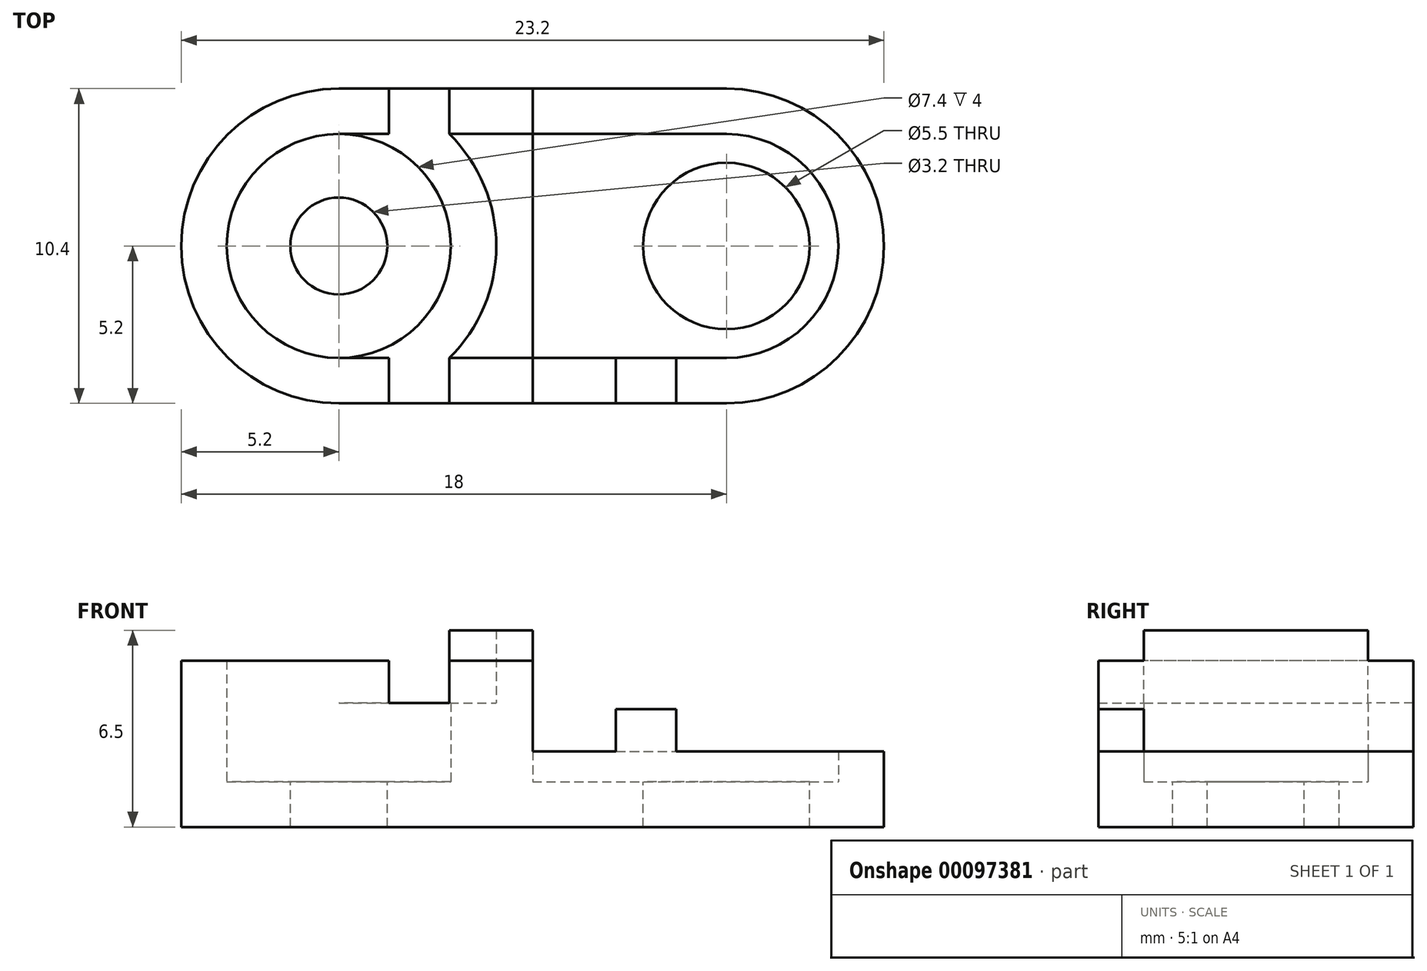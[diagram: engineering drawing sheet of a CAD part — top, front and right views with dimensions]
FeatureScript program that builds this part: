
annotation { "Feature Type Name" : "Feature", "Feature Type Description" : "" }
export const myFeature = defineFeature(function(context is Context, id is Id, definition is map)
    precondition{}
    {
        {
            var Q0;
            Q0=qCreatedBy(makeId("Top.planeOp"),FACE);
            var sketch = newSketch(context, id + "F0", { "sketchPlane" : qUnion([Q0])});
            skArc(sketch, "E0", {"start": v(-6.4, 5.2) * mm, "mid": v(-11.6, 0) * mm, "end": v(-6.4, -5.2) * mm});
            skArc(sketch, "E1", {"start": v(6.4, -5.2) * mm, "mid": v(11.6, 0) * mm, "end": v(6.4, 5.2) * mm});
            skLineSegment(sketch, "E2", {"start": v(0, -5.2) * mm, "end": v(0, 5.2) * mm, "construction": true});
            skLineSegment(sketch, "E3", {"start": v(-6.4, 5.2) * mm, "end": v(6.4, 5.2) * mm});
            skLineSegment(sketch, "E4", {"start": v(-6.4, -5.2) * mm, "end": v(6.4, -5.2) * mm});
            skSolve(sketch);
        }
        {
            var Q0;
            Q0 = qSketchRegion(id + "F0", true);
            extrude(context, id + "F1", {"entities" : qUnion([Q0]), "depth" : 1.5 * mm});
        }
        {
            var Q0;
            Q0=makeQuery(id+"F1.opExtrude","CAP_FACE",FACE,{"disambiguationData":[OSD([sQuery(id+"F0.wireOp",EDGE,"E0"),sQuery(id+"F0.wireOp",EDGE,"E1"),sQuery(id+"F0.wireOp",EDGE,"E3"),sQuery(id+"F0.wireOp",EDGE,"E4")])],"isStart":false});
            var sketch = newSketch(context, id + "F2", { "sketchPlane" : qUnion([Q0])});
            skLineSegment(sketch, "E5.0", {"start": v(-6.4, 5.2) * mm, "end": v(6.4, 5.2) * mm});
            skArc(sketch, "E5.1", {"start": v(-6.4, 5.2) * mm, "mid": v(-11.6, 0) * mm, "end": v(-6.4, -5.2) * mm});
            skLineSegment(sketch, "E5.2", {"start": v(-6.4, -5.2) * mm, "end": v(6.4, -5.2) * mm});
            skArc(sketch, "E5.3", {"start": v(6.4, -5.2) * mm, "mid": v(11.6, 0) * mm, "end": v(6.4, 5.2) * mm});
            skArc(sketch, "E6.0", {"start": v(-6.4, 3.7) * mm, "mid": v(-10.1, 0) * mm, "end": v(-6.4, -3.7) * mm});
            skLineSegment(sketch, "E6.1", {"start": v(-6.4, 3.7) * mm, "end": v(6.4, 3.7) * mm});
            skArc(sketch, "E6.2", {"start": v(6.4, -3.7) * mm, "mid": v(10.1, 0) * mm, "end": v(6.4, 3.7) * mm});
            skLineSegment(sketch, "E6.3", {"start": v(-6.4, -3.7) * mm, "end": v(6.4, -3.7) * mm});
            skLineSegment(sketch, "E7", {"start": v(0, -5.2) * mm, "end": v(0, -3.7) * mm});
            skLineSegment(sketch, "E8", {"start": v(0, -3.7) * mm, "end": v(0, 3.7) * mm, "construction": true});
            skLineSegment(sketch, "E9", {"start": v(0, 3.7) * mm, "end": v(0, 5.2) * mm});
            skSolve(sketch);
        }
        {
            var Q0;
            {var subQ3=sQuery(id+"F2.wireOp",EDGE,"E5.1");Q0=makeQuery(id+"F2.imprint","IMPRINT",FACE,{"disambiguationData":[TD([[makeQuery(id+"F2.imprint","IMPRINT",EDGE,{"derivedFrom":subQ3}),1.0]])]});}
            extrude(context, id + "F3", {"entities" : qUnion([Q0]), "operationType" : NewBodyOperationType.ADD, "depth" : 4 * mm});
        }
        {
            var Q0;
            {var subQ0=sQuery(id+"F2.wireOp",EDGE,"E5.3");Q0=makeQuery(id+"F2.imprint","IMPRINT",FACE,{"disambiguationData":[TD([[makeQuery(id+"F2.imprint","IMPRINT",EDGE,{"derivedFrom":subQ0}),1.0]])]});}
            extrude(context, id + "F4", {"entities" : qUnion([Q0]), "operationType" : NewBodyOperationType.ADD, "depth" : 1 * mm});
        }
        {
            var Q0;
            Q0=makeQuery(id+"Fe2mMpQbgtpmUDc_1.boolean.opBoolean","SPLIT",FACE,{"disambiguationData":[TD([makeQuery(id+"F3.opExtrude","SWEPT_FACE",FACE,{"disambiguationData":[OSD([sQuery(id+"F2.wireOp",EDGE,"af2ee723-1cb6-4ff9-9404-2c1013e4d717.1")])]})])],"derivedFrom":makeQuery(id+"F1.opExtrude","CAP_FACE",FACE,{"disambiguationData":[OSD([sQuery(id+"F0.wireOp",EDGE,"E0"),sQuery(id+"F0.wireOp",EDGE,"E1"),sQuery(id+"F0.wireOp",EDGE,"E3"),sQuery(id+"F0.wireOp",EDGE,"E4")])],"isStart":false})});
            var sketch = newSketch(context, id + "F5", { "sketchPlane" : qUnion([Q0])});
            skArc(sketch, "E10", {"start": v(-2.75, -3.7) * mm, "mid": v(-1.2, 0) * mm, "end": v(-2.75, 3.7) * mm});
            skArc(sketch, "E11", {"start": v(-6.4, -3.7) * mm, "mid": v(-2.7, 0) * mm, "end": v(-6.4, 3.7) * mm});
            skLineSegment(sketch, "E12.0", {"start": v(-6.4, 3.7) * mm, "end": v(-2.75, 3.7) * mm});
            skLineSegment(sketch, "E12.1", {"start": v(-6.4, -3.7) * mm, "end": v(-2.75, -3.7) * mm});
            skPoint(sketch, "E13.orphan", {"position": v(6.4, -3.7) * mm});
            skPoint(sketch, "E14.orphan", {"position": v(6.4, 3.7) * mm});
            skSolve(sketch);
        }
        {
            var Q0;
            Q0 = qSketchRegion(id + "F5", true);
            extrude(context, id + "F6", {"entities" : qUnion([Q0]), "operationType" : NewBodyOperationType.ADD, "depth" : 2.6 * mm});
        }
        {
            var Q0;
            {var subQ3=sQuery(id+"F2.wireOp",EDGE,"E6.0");Q0=makeQuery(id+"F2.imprint","IMPRINT",FACE,{"disambiguationData":[TD([[makeQuery(id+"F2.imprint","IMPRINT",EDGE,{"derivedFrom":subQ3}),1.0]])]});}
            var sketch = newSketch(context, id + "F7", { "sketchPlane" : qUnion([Q0])});
            skCircle(sketch, "E15", {"center": v(-6.4, 0) * mm, "radius": 1.6 * mm});
            skPoint(sketch, "E16.0", {"position": v(6.4, 0) * mm});
            skCircle(sketch, "E17", {"center": v(6.4, 0) * mm, "radius": 2.75 * mm});
            skSolve(sketch);
        }
        {
            var Q0;
            Q0 = qSketchRegion(id + "F7", true);
            extrude(context, id + "F8", {"entities" : qUnion([Q0]), "operationType" : NewBodyOperationType.REMOVE, "endBound" : BoundingType.THROUGH_ALL, "oppositeDirection" : true, "depth" : 25 * mm});
        }
        {
            var Q0;
            Q0=makeQuery(id+"F2.imprint","IMPRINT",FACE,{"disambiguationData":[TD([[makeQuery(id+"F2.imprint","IMPRINT",EDGE,{"derivedFrom":sQuery(id+"F2.wireOp",EDGE,"E6.0")}),1.0]])]});
            var sketch = newSketch(context, id + "F9", { "sketchPlane" : qUnion([Q0])});
            skLineSegment(sketch, "E18", {"start": v(0, -3.7) * mm, "end": v(0, 3.7) * mm});
            skCircle(sketch, "E19.0", {"center": v(6.4, 0) * mm, "radius": 2.75 * mm, "construction": true});
            skArc(sketch, "E20.0", {"start": v(-2.75, -3.7) * mm, "mid": v(-1.2, 0) * mm, "end": v(-2.75, 3.7) * mm});
            skLineSegment(sketch, "E20.1", {"start": v(-2.75, 3.7) * mm, "end": v(0, 3.7) * mm});
            skLineSegment(sketch, "E20.2", {"start": v(-2.75, -3.7) * mm, "end": v(0, -3.7) * mm});
            skSolve(sketch);
        }
        {
            var Q0;
            Q0 = qSketchRegion(id + "F9", true);
            extrude(context, id + "F10", {"entities" : qUnion([Q0]), "operationType" : NewBodyOperationType.ADD, "depth" : 5 * mm});
        }
        {
            var Q0;
            Q0=makeQuery(id+"F3.opExtrude","CAP_FACE",FACE,{"disambiguationData":[OSD([sQuery(id+"F2.wireOp",EDGE,"E5.0"),sQuery(id+"F2.wireOp",EDGE,"E5.1"),sQuery(id+"F2.wireOp",EDGE,"E5.2"),sQuery(id+"F2.wireOp",EDGE,"E6.0"),sQuery(id+"F2.wireOp",EDGE,"E6.1"),sQuery(id+"F2.wireOp",EDGE,"E6.3"),sQuery(id+"F2.wireOp",EDGE,"E7"),sQuery(id+"F2.wireOp",EDGE,"E9")])],"isStart":false});
            var sketch = newSketch(context, id + "F11", { "sketchPlane" : qUnion([Q0])});
            skLineSegment(sketch, "E21.bottom", {"start": v(-2.75, -3.7) * mm, "end": v(-4.75, -3.7) * mm});
            skLineSegment(sketch, "E21.top", {"start": v(-2.75, -5.2) * mm, "end": v(-4.75, -5.2) * mm});
            skLineSegment(sketch, "E21.left", {"start": v(-2.75, -3.7) * mm, "end": v(-2.75, -5.2) * mm});
            skLineSegment(sketch, "E21.right", {"start": v(-4.75, -3.7) * mm, "end": v(-4.75, -5.2) * mm});
            skLineSegment(sketch, "E22.bottom", {"start": v(-2.75, 3.7) * mm, "end": v(-4.75, 3.7) * mm});
            skLineSegment(sketch, "E22.top", {"start": v(-2.75, 5.2) * mm, "end": v(-4.75, 5.2) * mm});
            skLineSegment(sketch, "E22.left", {"start": v(-2.75, 3.7) * mm, "end": v(-2.75, 5.2) * mm});
            skLineSegment(sketch, "E22.right", {"start": v(-4.75, 3.7) * mm, "end": v(-4.75, 5.2) * mm});
            skSolve(sketch);
        }
        {
            var Q0;
            Q0 = qSketchRegion(id + "F11", true);
            var Q1;
            Q1=makeQuery(id+"F6.opExtrude","CAP_FACE",FACE,{"disambiguationData":[OSD([sQuery(id+"F5.wireOp",EDGE,"E10"),sQuery(id+"F5.wireOp",EDGE,"E11"),sQuery(id+"F5.wireOp",EDGE,"E12.0"),sQuery(id+"F5.wireOp",EDGE,"E12.1")])],"isStart":false});
            extrude(context, id + "F12", {"entities" : qUnion([Q0]), "operationType" : NewBodyOperationType.REMOVE, "endBound" : BoundingType.UP_TO_SURFACE, "oppositeDirection" : true, "endBoundEntityFace" : qUnion([Q1]), "depth" : 2 * mm});
        }
        {
            var Q0;
            Q0=makeQuery(id+"F4.opExtrude","CAP_FACE",FACE,{"disambiguationData":[OSD([sQuery(id+"F2.wireOp",EDGE,"E5.0"),sQuery(id+"F2.wireOp",EDGE,"E5.2"),sQuery(id+"F2.wireOp",EDGE,"E5.3"),sQuery(id+"F2.wireOp",EDGE,"E6.1"),sQuery(id+"F2.wireOp",EDGE,"E6.2"),sQuery(id+"F2.wireOp",EDGE,"E6.3"),sQuery(id+"F2.wireOp",EDGE,"E7"),sQuery(id+"F2.wireOp",EDGE,"E9")])],"isStart":false});
            var sketch = newSketch(context, id + "F13", { "sketchPlane" : qUnion([Q0])});
            skArc(sketch, "E23.MirrorCS", {"start": v(2.75, -3.7) * mm, "mid": v(1.2, 0) * mm, "end": v(2.75, 3.7) * mm, "construction": true});
            skLineSegment(sketch, "E24.bottom", {"start": v(2.75, -3.7) * mm, "end": v(4.75, -3.7) * mm});
            skLineSegment(sketch, "E24.top", {"start": v(2.75, -5.2) * mm, "end": v(4.75, -5.2) * mm});
            skLineSegment(sketch, "E24.left", {"start": v(2.75, -3.7) * mm, "end": v(2.75, -5.2) * mm});
            skLineSegment(sketch, "E24.right", {"start": v(4.75, -3.7) * mm, "end": v(4.75, -5.2) * mm});
            skLineSegment(sketch, "E25.bottom", {"start": v(2.75, 3.7) * mm, "end": v(4.75, 3.7) * mm});
            skLineSegment(sketch, "E25.top", {"start": v(2.75, 5.2) * mm, "end": v(4.75, 5.2) * mm});
            skLineSegment(sketch, "E25.left", {"start": v(2.75, 3.7) * mm, "end": v(2.75, 5.2) * mm});
            skLineSegment(sketch, "E25.right", {"start": v(4.75, 3.7) * mm, "end": v(4.75, 5.2) * mm});
            skSolve(sketch);
        }
        {
            var Q0;
            Q0=makeQuery(id+"F13.imprint","IMPRINT",FACE,{"disambiguationData":[TD([[makeQuery(id+"F13.imprint","IMPRINT",EDGE,{"derivedFrom":sQuery(id+"F13.wireOp",EDGE,"E24.bottom")}),-1.0]])]});
            extrude(context, id + "F14", {"entities" : qUnion([Q0]), "operationType" : NewBodyOperationType.ADD, "depth" : 1.4 * mm});
        }
    });
